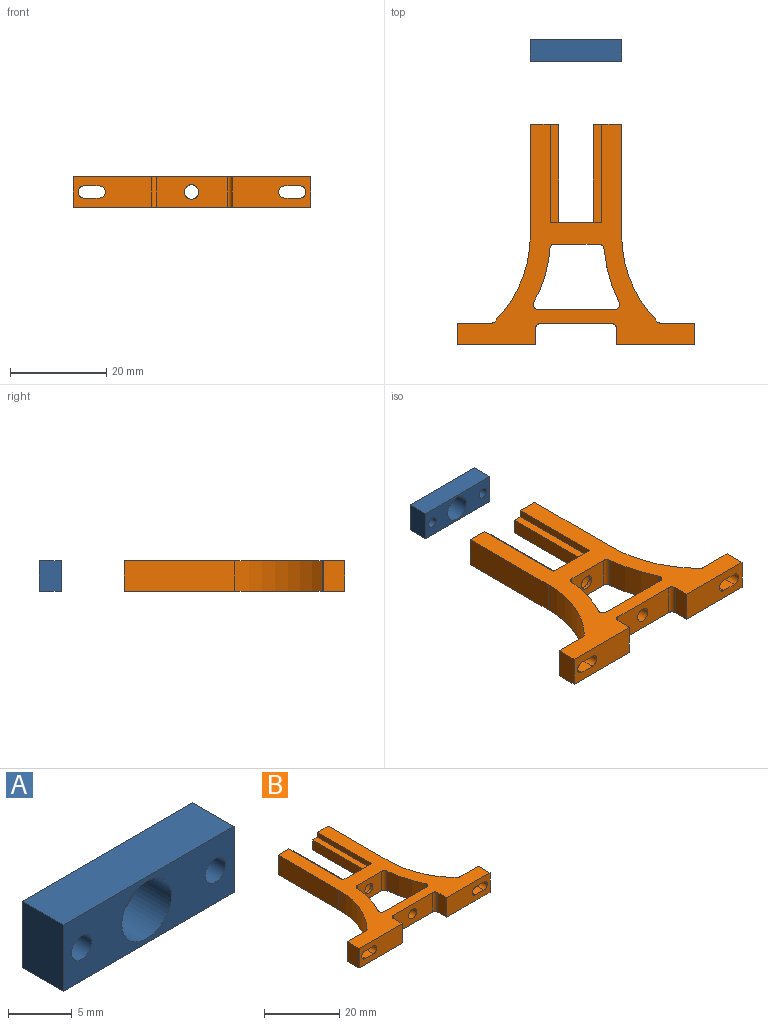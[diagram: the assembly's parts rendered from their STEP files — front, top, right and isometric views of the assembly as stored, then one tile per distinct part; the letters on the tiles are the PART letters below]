
ASSEMBLY  parts=2 mates=2
PART A: 11 faces, bbox 18.9x4.5x6.4 mm
  f0: cylinder r=1.5mm len=3mm, axis (0,1,0), area 7.4mm2, adj f7,f9
  f1: cylinder r=1.12mm len=4.54mm, axis (0,1,0), area 32.1mm2, adj f2,f7
  f2: plane 18.92x6.35mm, normal (0,-1,0), area 88.5mm2, adj f1,f3,f4,f5,f6,f8,f10
  f3: plane 18.92x4.54mm, normal (0,0,-1), area 85.9mm2, adj f2,f5,f6,f7
  f4: plane 18.92x4.54mm, normal (0,0,1), area 85.9mm2, adj f2,f5,f6,f7
  f5: plane 6.35x4.54mm, normal (-1,0,0), area 28.8mm2, adj f2,f3,f4,f7
  f6: plane 6.35x4.54mm, normal (1,0,0), area 28.8mm2, adj f2,f3,f4,f7
  f7: plane 18.92x6.35mm, normal (0,1,0), area 105.1mm2, adj f0,f1,f3,f4,f5,f6,f8
  f8: cylinder r=1.12mm len=4.54mm, axis (0,1,0), area 32.1mm2, adj f2,f7
  f9: plane 5.5x5.5mm, normal (0,-1,0), area 16.7mm2, adj f0,f10
  f10: cylinder r=2.75mm len=5.5mm, axis (0,-1,0), area 64.8mm2, adj f2,f9
PART B: 58 faces, bbox 49.3x45.7x6.4 mm
  f0: cylinder r=1.5mm len=3mm, axis (0,1,0), area 7.1mm2, adj f17,f41
  f1: plane 10.67x6.35mm, normal (0,1,0), area 32.6mm2, adj f14,f18,f21,f22,f23,f24,f25,f26
  f2: plane 6.96x6.35mm, normal (0,1,0), area 31.4mm2, adj f20,f21,f28,f46,f50,f51,f52,f53
  f3: cylinder r=25.67mm len=18.14mm, axis (0,0,-1), area 127.9mm2, adj f4,f21,f28,f46
  f4: plane 22.86x6.35mm, normal (1,0,0), area 145.2mm2, adj f3,f21,f28,f31
  f5: plane 22.86x6.35mm, normal (-1,0,0), area 145.2mm2, adj f6,f21,f28,f32
  f6: cylinder r=25.67mm len=18.14mm, axis (0,0,-1), area 127.9mm2, adj f5,f21,f28,f47
  f7: plane 6.96x6.35mm, normal (0,1,0), area 31.4mm2, adj f8,f21,f28,f47,f54,f55,f56,f57
  f8: plane 6.35x4.38mm, normal (-1,0,0), area 27.8mm2, adj f7,f9,f21,f28
  f9: plane 16.26x6.35mm, normal (0,-1,0), area 90.4mm2, adj f8,f10,f21,f28,f54,f55,f56,f57
  f10: plane 6.35x3.38mm, normal (1,0,0), area 21.4mm2, adj f9,f21,f28,f48
  f11: plane 14.76x6.35mm, normal (0,-1,0), area 86.7mm2, adj f21,f28,f39,f48,f49
  f12: plane 6.35x3.38mm, normal (-1,0,0), area 21.4mm2, adj f13,f21,f28,f49
  f13: plane 16.26x6.35mm, normal (0,-1,0), area 90.4mm2, adj f12,f20,f21,f28,f50,f51,f52,f53
  f14: plane 20.32x1.57mm, normal (-1,0,0), area 32mm2, adj f1,f21,f25,f31
  f15: plane 15.91x6.35mm, normal (0,1,0), area 94mm2, adj f21,f28,f39,f42,f45
  f16: cylinder r=27.15mm len=11.14mm, axis (0,0,-1), area 74.4mm2, adj f21,f28,f42,f43
  f17: plane 9.19x6.35mm, normal (0,-1,0), area 51.3mm2, adj f0,f21,f28,f43,f44
  f18: plane 20.32x1.57mm, normal (1,0,0), area 32mm2, adj f1,f21,f23,f32
  f19: cylinder r=32.95mm len=11.21mm, axis (0,0,-1), area 74.3mm2, adj f21,f28,f44,f45
  f20: plane 6.35x4.38mm, normal (1,0,0), area 27.8mm2, adj f2,f13,f21,f28
  f21: plane 49.28x45.67mm, normal (0,0,1), area 608.7mm2, adj f1,f2,f3,f4,f5,f6,f7,f8
  f22: plane 20.32x3.2mm, normal (1,0,0), area 65mm2, adj f1,f23,f29,f32
  f23: plane 20.32x1.78mm, normal (0,0,1), area 36.1mm2, adj f1,f18,f22,f32
  f24: plane 20.32x3.2mm, normal (-1,0,0), area 65mm2, adj f1,f25,f30,f31
  f25: plane 20.32x1.78mm, normal (0,0,1), area 36.1mm2, adj f1,f14,f24,f31
  f26: plane 20.32x1.57mm, normal (-1,0,0), area 32mm2, adj f1,f28,f30,f31
  f27: plane 20.32x1.57mm, normal (1,0,0), area 32mm2, adj f1,f28,f29,f32
  f28: plane 49.28x45.67mm, normal (0,0,-1), area 608.7mm2, adj f1,f2,f3,f4,f5,f6,f7,f8
  f29: plane 20.32x1.78mm, normal (0,0,-1), area 36.1mm2, adj f1,f22,f27,f32
  f30: plane 20.32x1.78mm, normal (0,0,-1), area 36.1mm2, adj f1,f24,f26,f31
  f31: plane 6.35x5.91mm, normal (0,1,0), area 23.6mm2, adj f4,f14,f21,f24,f25,f26,f28,f30
  f32: plane 6.35x5.91mm, normal (0,1,0), area 23.6mm2, adj f5,f18,f21,f22,f23,f27,f28,f29
  f33: cylinder r=1.12mm len=2.25mm, axis (0,1,0), area 2mm2, adj f35,f38
  f34: cylinder r=1.62mm len=3.25mm, axis (0,1,0), area 28.1mm2, adj f31,f35
  f35: plane 3.25x3.25mm, normal (0,1,0), area 4.3mm2, adj f33,f34
  f36: cylinder r=1.62mm len=3.25mm, axis (0,1,0), area 28.1mm2, adj f32,f37
  f37: plane 3.25x3.25mm, normal (0,1,0), area 8.3mm2, adj f36
  f38: plane 2.25x2.25mm, normal (0,1,0), area 4mm2, adj f33
  f39: cylinder r=1.5mm len=3mm, axis (0,1,0), area 27.6mm2, adj f11,f15
  f40: cylinder r=2.75mm len=5.5mm, axis (0,1,0), area 64.8mm2, adj f1,f41
  f41: plane 5.5x5.5mm, normal (0,1,0), area 16.7mm2, adj f0,f40
  f42: cylinder r=1mm len=6.35mm, axis (0,0,-1), area 13.2mm2, adj f15,f16,f21,f28
  f43: cylinder r=1mm len=6.35mm, axis (0,0,-1), area 9.5mm2, adj f16,f17,f21,f28
  f44: cylinder r=1mm len=6.35mm, axis (0,0,-1), area 9.4mm2, adj f17,f19,f21,f28
  f45: cylinder r=1mm len=6.35mm, axis (0,0,-1), area 12.8mm2, adj f15,f19,f21,f28
  f46: cylinder r=1mm len=6.35mm, axis (0,0,-1), area 5mm2, adj f2,f3,f21,f28
  f47: cylinder r=1mm len=6.35mm, axis (0,0,-1), area 5mm2, adj f6,f7,f21,f28
  f48: cylinder r=1mm len=6.35mm, axis (0,0,1), area 10mm2, adj f10,f11,f21,f28
  f49: cylinder r=1mm len=6.35mm, axis (0,0,-1), area 10mm2, adj f11,f12,f21,f28
  f50: cylinder r=1.27mm len=4.38mm, axis (0,-1,0), area 17.5mm2, adj f2,f13,f51,f52
  f51: plane 4.38x3.07mm, normal (0,0,-1), area 13.4mm2, adj f2,f13,f50,f53
  f52: plane 4.38x3.07mm, normal (0,0,1), area 13.4mm2, adj f2,f13,f50,f53
  f53: cylinder r=1.27mm len=4.38mm, axis (0,-1,0), area 17.5mm2, adj f2,f13,f51,f52
  f54: cylinder r=1.27mm len=4.38mm, axis (0,-1,0), area 17.5mm2, adj f7,f9,f55,f56
  f55: plane 4.38x3.07mm, normal (0,0,-1), area 13.4mm2, adj f7,f9,f54,f57
  f56: plane 4.38x3.07mm, normal (0,0,1), area 13.4mm2, adj f7,f9,f54,f57
  f57: cylinder r=1.27mm len=4.38mm, axis (0,-1,0), area 17.5mm2, adj f7,f9,f55,f56
PLACE A t=(-27.28,18.47,-12.82)mm
PLACE B t=(-27.28,5.36,-12.82)mm fixed
MATE cylindrical A.f0 <-> B.f0  axis (0,1,0) through (-27.38,33.17,-12.82)mm
MATE planar B.f21 <-> A.f4  axis (0,0,1) through (-21.94,5.36,-9.64)mm
